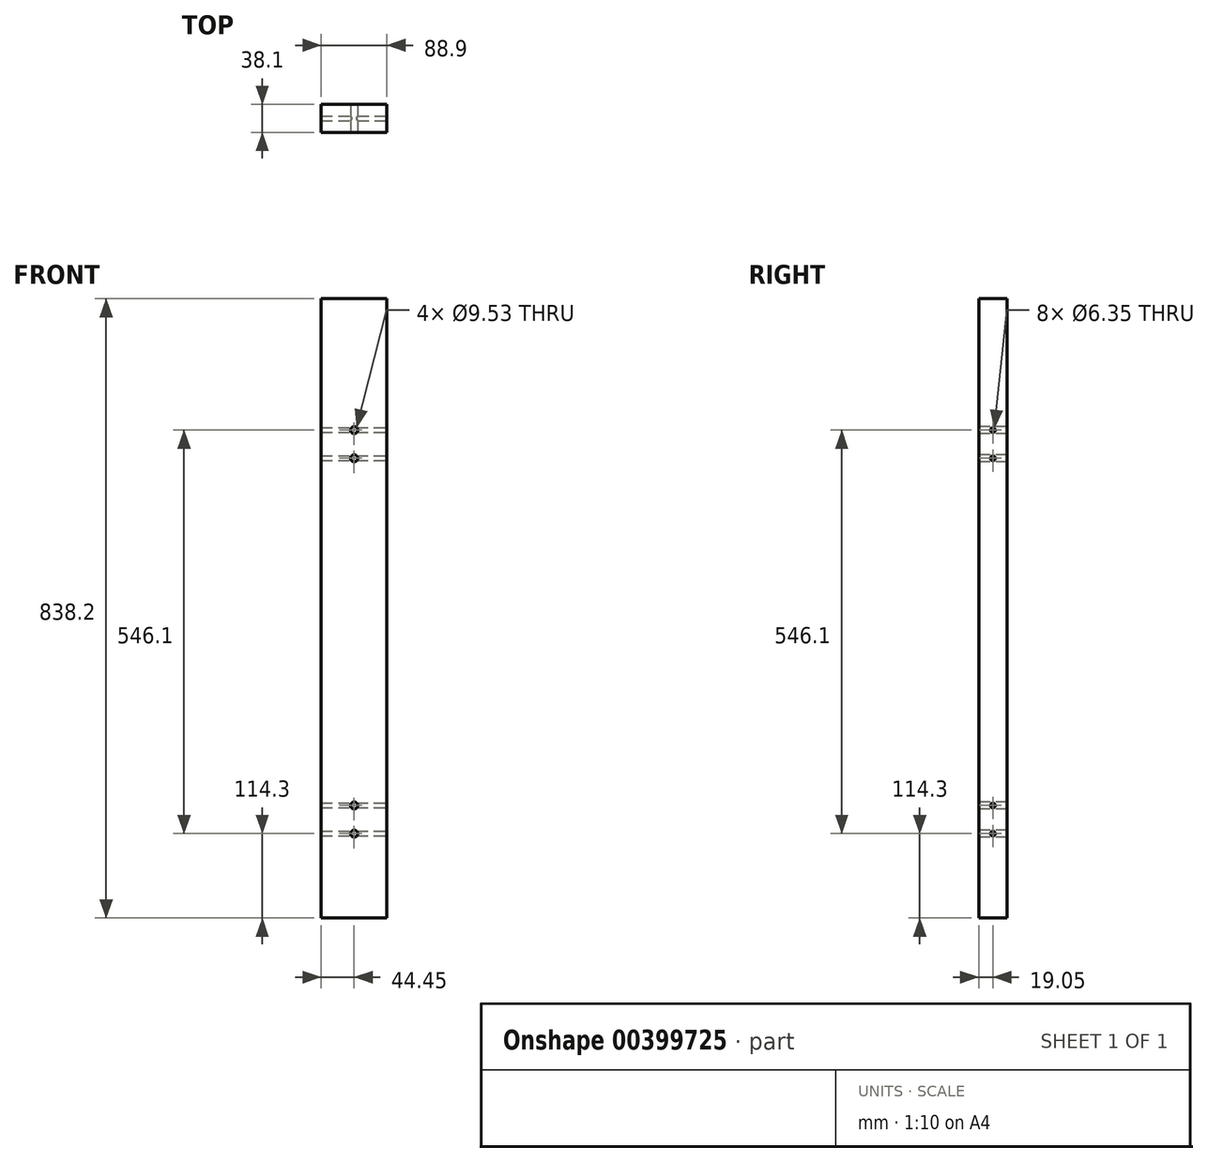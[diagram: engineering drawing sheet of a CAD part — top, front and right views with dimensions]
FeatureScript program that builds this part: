
annotation { "Feature Type Name" : "Feature", "Feature Type Description" : "" }
export const myFeature = defineFeature(function(context is Context, id is Id, definition is map)
    precondition{}
    {
        {
            var Q0;
            Q0=qCreatedBy(makeId("Top.planeOp"),FACE);
            var sketch = newSketch(context, id + "F0", { "sketchPlane" : qUnion([Q0])});
            skLineSegment(sketch, "E0.bottom", {"start": v(-44.45, 19.05) * mm, "end": v(44.45, 19.05) * mm});
            skLineSegment(sketch, "E0.top", {"start": v(-44.45, -19.05) * mm, "end": v(44.45, -19.05) * mm});
            skLineSegment(sketch, "E0.left", {"start": v(-44.45, 19.05) * mm, "end": v(-44.45, -19.05) * mm});
            skLineSegment(sketch, "E0.right", {"start": v(44.45, 19.05) * mm, "end": v(44.45, -19.05) * mm});
            skSolve(sketch);
        }
        {
            var Q0;
            Q0 = qSketchRegion(id + "F0", true);
            extrude(context, id + "F1", {"entities" : qUnion([Q0]), "endBound" : BoundingType.SYMMETRIC, "depth" : 838.2 * mm});
        }
        {
            var Q0;
            Q0=makeQuery(id+"F1.opExtrude","SWEPT_FACE",FACE,{"disambiguationData":[OSD([sQuery(id+"F0.wireOp",EDGE,"E0.top")])]});
            var sketch = newSketch(context, id + "F2", { "sketchPlane" : qUnion([Q0])});
            skCircle(sketch, "E1", {"center": v(0, 241.3) * mm, "radius": 4.76 * mm});
            skCircle(sketch, "E2", {"center": v(0, 203.2) * mm, "radius": 4.76 * mm});
            skCircle(sketch, "E3", {"center": v(0, -266.7) * mm, "radius": 4.76 * mm});
            skCircle(sketch, "E4", {"center": v(0, -304.8) * mm, "radius": 4.76 * mm});
            skSolve(sketch);
        }
        {
            var Q0;
            Q0 = qSketchRegion(id + "F2", true);
            extrude(context, id + "F3", {"entities" : qUnion([Q0]), "operationType" : NewBodyOperationType.REMOVE, "endBound" : BoundingType.THROUGH_ALL, "oppositeDirection" : true, "depth" : 25.4 * mm});
        }
        {
            var Q0;
            Q0=makeQuery(id+"F1.opExtrude","SWEPT_FACE",FACE,{"disambiguationData":[OSD([sQuery(id+"F0.wireOp",EDGE,"E0.right")])]});
            var sketch = newSketch(context, id + "F4", { "sketchPlane" : qUnion([Q0])});
            skCircle(sketch, "E5", {"center": v(0, 241.3) * mm, "radius": 3.18 * mm});
            skCircle(sketch, "E6", {"center": v(0, 203.2) * mm, "radius": 3.18 * mm});
            skCircle(sketch, "E7", {"center": v(0, -304.8) * mm, "radius": 3.18 * mm});
            skCircle(sketch, "E8", {"center": v(0, -266.7) * mm, "radius": 3.18 * mm});
            skSolve(sketch);
        }
        {
            var Q0;
            Q0 = qSketchRegion(id + "F4", true);
            extrude(context, id + "F5", {"entities" : qUnion([Q0]), "operationType" : NewBodyOperationType.REMOVE, "endBound" : BoundingType.THROUGH_ALL, "oppositeDirection" : true, "depth" : 38.1 * mm});
        }
    });
